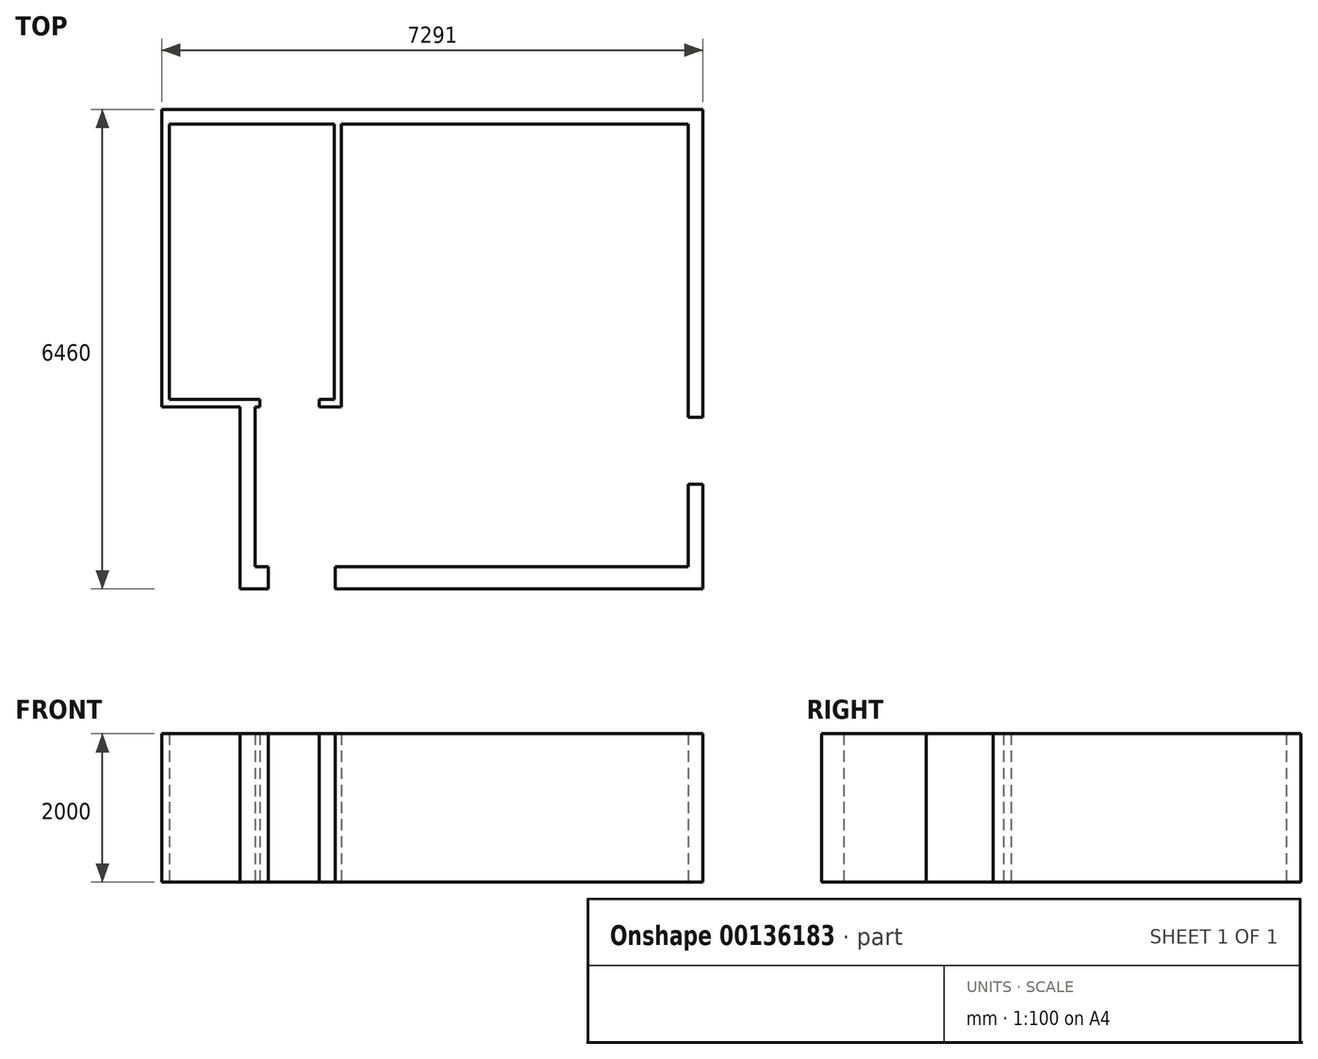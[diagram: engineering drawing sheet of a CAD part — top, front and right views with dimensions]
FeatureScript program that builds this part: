
annotation { "Feature Type Name" : "Feature", "Feature Type Description" : "" }
export const myFeature = defineFeature(function(context is Context, id is Id, definition is map)
    precondition{}
    {
        {
            var Q0;
            Q0=qCreatedBy(makeId("Top.planeOp"),FACE);
            var sketch = newSketch(context, id + "F0", { "sketchPlane" : qUnion([Q0])});
            skLineSegment(sketch, "E0", {"start": v(0, 0) * mm, "end": v(0, 1410) * mm});
            skLineSegment(sketch, "E1", {"start": v(0, 1410) * mm, "end": v(-200, 1410) * mm});
            skLineSegment(sketch, "E2", {"start": v(-200, 1410) * mm, "end": v(-200, 300) * mm});
            skLineSegment(sketch, "E3", {"start": v(-200, 300) * mm, "end": v(-4954, 300) * mm});
            skLineSegment(sketch, "E4", {"start": v(-4954, 300) * mm, "end": v(-4954, 0) * mm});
            skLineSegment(sketch, "E5", {"start": v(-4954, 0) * mm, "end": v(0, 0) * mm});
            skLineSegment(sketch, "E6", {"start": v(0, 2310) * mm, "end": v(0, 6460) * mm});
            skLineSegment(sketch, "E7", {"start": v(0, 6460) * mm, "end": v(-7291, 6460) * mm});
            skLineSegment(sketch, "E8", {"start": v(-7291, 6460) * mm, "end": v(-7291, 2452) * mm});
            skLineSegment(sketch, "E9", {"start": v(-7291, 2452) * mm, "end": v(-6234, 2452) * mm});
            skLineSegment(sketch, "E10", {"start": v(-6234, 2452) * mm, "end": v(-6234, 0) * mm});
            skLineSegment(sketch, "E11", {"start": v(-6234, 0) * mm, "end": v(-5854, 0) * mm});
            skLineSegment(sketch, "E12", {"start": v(-5854, 0) * mm, "end": v(-5854, 300) * mm});
            skLineSegment(sketch, "E13", {"start": v(-5854, 300) * mm, "end": v(-6034, 300) * mm});
            skLineSegment(sketch, "E14", {"start": v(-6034, 300) * mm, "end": v(-6034, 2452) * mm});
            skLineSegment(sketch, "E15", {"start": v(-6034, 2452) * mm, "end": v(-5969, 2452) * mm});
            skLineSegment(sketch, "E16", {"start": v(-5969, 2452) * mm, "end": v(-5969, 2552) * mm});
            skLineSegment(sketch, "E17", {"start": v(-5969, 2552) * mm, "end": v(-7191, 2552) * mm});
            skLineSegment(sketch, "E18", {"start": v(-7191, 2552) * mm, "end": v(-7191, 6260) * mm});
            skLineSegment(sketch, "E19", {"start": v(-7191, 6260) * mm, "end": v(-4969, 6260) * mm});
            skLineSegment(sketch, "E20", {"start": v(-4969, 6260) * mm, "end": v(-4969, 2552) * mm});
            skLineSegment(sketch, "E21", {"start": v(-4969, 2552) * mm, "end": v(-5169, 2552) * mm});
            skLineSegment(sketch, "E22", {"start": v(-5169, 2552) * mm, "end": v(-5169, 2452) * mm});
            skLineSegment(sketch, "E23", {"start": v(-5169, 2452) * mm, "end": v(-4869, 2452) * mm});
            skLineSegment(sketch, "E24", {"start": v(-4869, 2452) * mm, "end": v(-4869, 6260) * mm});
            skLineSegment(sketch, "E25", {"start": v(-4869, 6260) * mm, "end": v(-200, 6260) * mm});
            skLineSegment(sketch, "E26", {"start": v(-200, 6260) * mm, "end": v(-200, 2310) * mm});
            skLineSegment(sketch, "E27", {"start": v(-200, 2310) * mm, "end": v(0, 2310) * mm});
            skSolve(sketch);
        }
        {
            var Q0;
            Q0 = qSketchRegion(id + "F0", true);
            extrude(context, id + "F1", {"entities" : qUnion([Q0]), "depth" : 2000 * mm});
        }
    });
